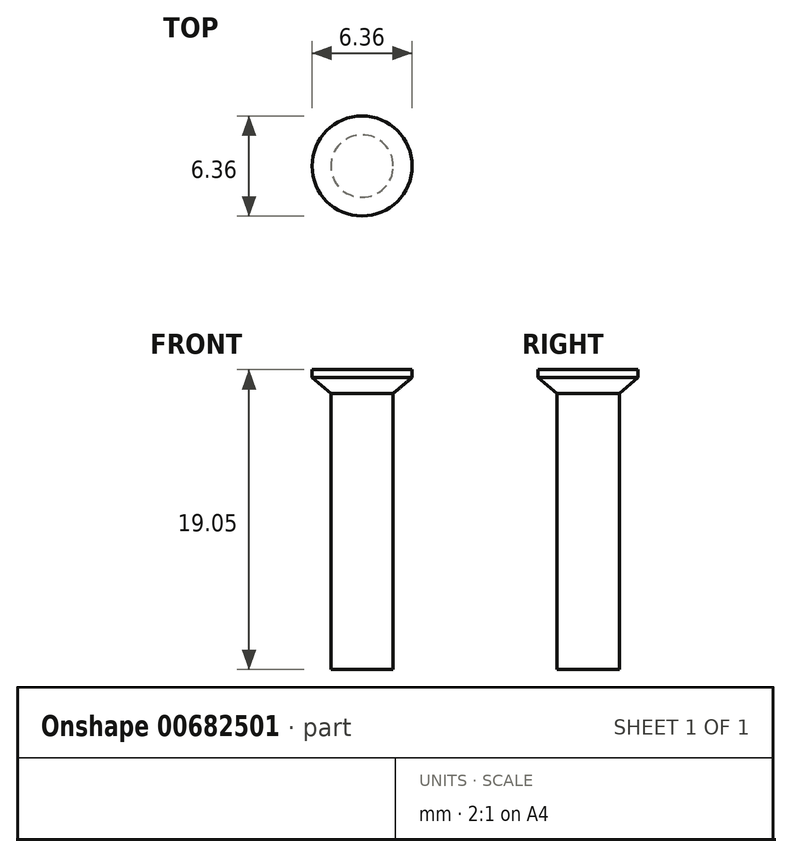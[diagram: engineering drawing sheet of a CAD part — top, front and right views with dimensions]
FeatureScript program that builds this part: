
annotation { "Feature Type Name" : "Feature", "Feature Type Description" : "" }
export const myFeature = defineFeature(function(context is Context, id is Id, definition is map)
    precondition{}
    {
        {
            var Q0;
            Q0=qCreatedBy(makeId("Front.planeOp"),FACE);
            var sketch = newSketch(context, id + "F0", { "sketchPlane" : qUnion([Q0])});
            skLineSegment(sketch, "E0", {"start": v(0, 0) * mm, "end": v(-3.17, 0) * mm});
            skLineSegment(sketch, "E1", {"start": v(-3.17, 0) * mm, "end": v(-3.17, -0.5) * mm});
            skLineSegment(sketch, "E2", {"start": v(-3.17, -0.5) * mm, "end": v(-1.98, -1.5) * mm});
            skLineSegment(sketch, "E3", {"start": v(-1.98, -1.5) * mm, "end": v(-1.98, -19.05) * mm});
            skLineSegment(sketch, "E4", {"start": v(-1.98, -19.05) * mm, "end": v(0, -19.05) * mm});
            skLineSegment(sketch, "E5", {"start": v(0, -19.05) * mm, "end": v(0, 0) * mm});
            skLineSegment(sketch, "E6", {"start": v(-3.17, -0.5) * mm, "end": v(19.48, -0.5) * mm, "construction": true});
            skLineSegment(sketch, "E7", {"start": v(-1.98, -1.5) * mm, "end": v(-1.98, -0.5) * mm, "construction": true});
            skLineSegment(sketch, "E8", {"start": v(0, 91.25) * mm, "end": v(0, -34.46) * mm, "construction": true});
            skSolve(sketch);
        }
        {
            var Q0;
            Q0 = qSketchRegion(id + "F0", true);
            var Q1;
            Q1=sQuery(id+"F0.wireOp",EDGE,"E8");
            revolve(context, id + "F1", {"entities" : qUnion([Q0]), "axis" : qUnion([Q1]), "revolveType" : RevolveType.FULL});
        }
    });
